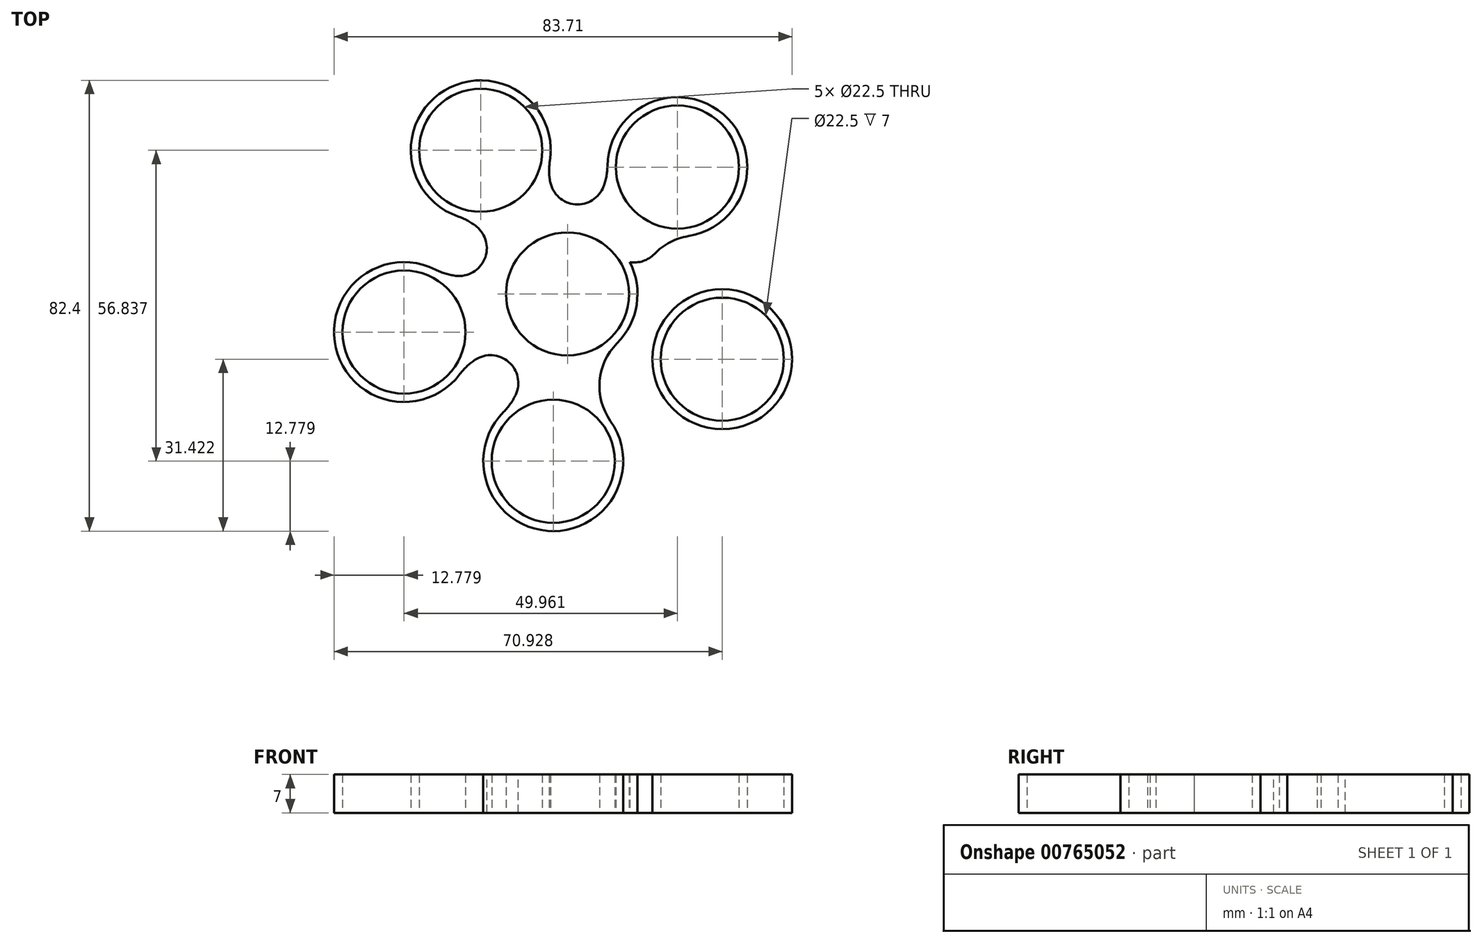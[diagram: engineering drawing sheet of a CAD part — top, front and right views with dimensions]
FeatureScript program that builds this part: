
annotation { "Feature Type Name" : "Feature", "Feature Type Description" : "" }
export const myFeature = defineFeature(function(context is Context, id is Id, definition is map)
    precondition{}
    {
        {
            var Q0;
            Q0=qCreatedBy(makeId("Top.planeOp"),FACE);
            var sketch = newSketch(context, id + "F0", { "sketchPlane" : qUnion([Q0])});
            skCircle(sketch, "E0", {"center": v(0, 0) * mm, "radius": 12.78 * mm});
            skCircle(sketch, "E1", {"center": v(20.08, 23.2) * mm, "radius": 12.78 * mm});
            skArc(sketch, "E2", {"start": v(22.1, 10.58) * mm, "mid": v(15.48, 6.89) * mm, "end": v(12.78, -0.2) * mm});
            skArc(sketch, "E3.MirrorCS", {"start": v(7.3, 23.4) * mm, "mid": v(4.6, 16.31) * mm, "end": v(-2.03, 12.62) * mm});
            skCircle(sketch, "E4", {"center": v(0, 0) * mm, "radius": 11.25 * mm});
            skCircle(sketch, "E5", {"center": v(20.08, 23.2) * mm, "radius": 11.25 * mm});
            skCircle(sketch, "E6.1.0", {"center": v(-15.86, 26.27) * mm, "radius": 11.25 * mm});
            skCircle(sketch, "E6.1.1", {"center": v(-15.86, 26.27) * mm, "radius": 12.78 * mm});
            skArc(sketch, "E6.1.2", {"start": v(-3.23, 24.3) * mm, "mid": v(-1.76, 16.85) * mm, "end": v(4.14, 12.1) * mm});
            skArc(sketch, "E6.1.3", {"start": v(-20, 14.17) * mm, "mid": v(-14.1, 9.41) * mm, "end": v(-12.63, 1.97) * mm});
            skCircle(sketch, "E6.2.0", {"center": v(-29.88, -6.97) * mm, "radius": 11.25 * mm});
            skCircle(sketch, "E6.2.1", {"center": v(-29.88, -6.97) * mm, "radius": 12.78 * mm});
            skArc(sketch, "E6.2.2", {"start": v(-24.1, 4.44) * mm, "mid": v(-16.58, 3.53) * mm, "end": v(-10.23, 7.67) * mm});
            skArc(sketch, "E6.2.3", {"start": v(-19.65, -14.64) * mm, "mid": v(-13.3, -10.5) * mm, "end": v(-5.78, -11.4) * mm});
            skCircle(sketch, "E6.3.0", {"center": v(-2.6, -30.57) * mm, "radius": 11.25 * mm});
            skCircle(sketch, "E6.3.1", {"center": v(-2.6, -30.57) * mm, "radius": 12.78 * mm});
            skArc(sketch, "E6.3.2", {"start": v(-11.67, -21.55) * mm, "mid": v(-8.48, -14.67) * mm, "end": v(-10.46, -7.35) * mm});
            skArc(sketch, "E6.3.3", {"start": v(7.85, -23.22) * mm, "mid": v(5.87, -15.9) * mm, "end": v(9.06, -9.02) * mm});
            skCircle(sketch, "E6.4.0", {"center": v(28.27, -11.93) * mm, "radius": 11.25 * mm});
            skCircle(sketch, "E6.4.1", {"center": v(28.27, -11.93) * mm, "radius": 12.78 * mm});
            skArc(sketch, "E6.4.2", {"start": v(16.89, -17.76) * mm, "mid": v(11.33, -12.6) * mm, "end": v(3.76, -12.22) * mm});
            skArc(sketch, "E6.4.3", {"start": v(24.5, 0.29) * mm, "mid": v(16.93, 0.67) * mm, "end": v(11.38, 5.83) * mm});
            skSolve(sketch);
        }
        {
            var Q0;
            {var subQ3=sQuery(id+"F0.wireOp",EDGE,"E3.MirrorCS");var subQ7=sQuery(id+"F0.wireOp",EDGE,"E0");var subQ8=makeQuery(id+"F0.imprint","INTERSECT",VERTEX,{"derivedFrom":[subQ7,subQ3]});Q0=makeQuery(id+"F0.imprint","IMPRINT",FACE,{"disambiguationData":[TD([[makeQuery(id+"F0.imprint","IMPRINT",EDGE,{"disambiguationData":[TD([[subQ8,-1.0]])],"derivedFrom":subQ7}),-1.0]])]});}
            var Q1;
            {var subQ1=sQuery(id+"F0.wireOp",EDGE,"E0");var subQ13=makeQuery(id+"F0.imprint","INTERSECT",VERTEX,{"derivedFrom":[subQ1,sQuery(id+"F0.wireOp",EDGE,"E6.1.2")]});Q1=makeQuery(id+"F0.imprint","IMPRINT",FACE,{"disambiguationData":[TD([[makeQuery(id+"F0.imprint","IMPRINT",EDGE,{"disambiguationData":[TD([[subQ13,1.0]])],"derivedFrom":subQ1}),1.0]])]});}
            var Q2;
            {var subQ0=sQuery(id+"F0.wireOp",EDGE,"E3.MirrorCS");var subQ1=sQuery(id+"F0.wireOp",EDGE,"E0");var subQ2=makeQuery(id+"F0.imprint","INTERSECT",VERTEX,{"derivedFrom":[subQ1,subQ0]});Q2=makeQuery(id+"F0.imprint","IMPRINT",FACE,{"disambiguationData":[TD([[makeQuery(id+"F0.imprint","IMPRINT",EDGE,{"disambiguationData":[TD([[subQ2,1.0]])],"derivedFrom":subQ1}),-1.0]])]});}
            var Q3;
            {var subQ1=sQuery(id+"F0.wireOp",EDGE,"E0");var subQ3=sQuery(id+"F0.wireOp",EDGE,"E6.4.3");var subQ4=makeQuery(id+"F0.imprint","INTERSECT",VERTEX,{"derivedFrom":[subQ1,subQ3]});Q3=makeQuery(id+"F0.imprint","IMPRINT",FACE,{"disambiguationData":[TD([[makeQuery(id+"F0.imprint","IMPRINT",EDGE,{"disambiguationData":[TD([[subQ4,1.0]])],"derivedFrom":subQ3}),1.0]])]});}
            var Q4;
            {var subQ1=sQuery(id+"F0.wireOp",EDGE,"E0");var subQ8=makeQuery(id+"F0.imprint","INTERSECT",VERTEX,{"derivedFrom":[subQ1,sQuery(id+"F0.wireOp",EDGE,"E6.4.3")]});Q4=makeQuery(id+"F0.imprint","IMPRINT",FACE,{"disambiguationData":[TD([[makeQuery(id+"F0.imprint","IMPRINT",EDGE,{"disambiguationData":[TD([[subQ8,-1.0]])],"derivedFrom":subQ1}),1.0]])]});}
            var Q5;
            {var subQ0=sQuery(id+"F0.wireOp",EDGE,"E6.1.3");var subQ1=sQuery(id+"F0.wireOp",EDGE,"E0");var subQ2=makeQuery(id+"F0.imprint","INTERSECT",VERTEX,{"derivedFrom":[subQ1,subQ0]});Q5=makeQuery(id+"F0.imprint","IMPRINT",FACE,{"disambiguationData":[TD([[makeQuery(id+"F0.imprint","IMPRINT",EDGE,{"disambiguationData":[TD([[subQ2,1.0]])],"derivedFrom":subQ1}),-1.0]])]});}
            var Q6;
            {var subQ3=sQuery(id+"F0.wireOp",EDGE,"E6.1.3");var subQ7=sQuery(id+"F0.wireOp",EDGE,"E0");var subQ8=makeQuery(id+"F0.imprint","INTERSECT",VERTEX,{"derivedFrom":[subQ7,subQ3]});Q6=makeQuery(id+"F0.imprint","IMPRINT",FACE,{"disambiguationData":[TD([[makeQuery(id+"F0.imprint","IMPRINT",EDGE,{"disambiguationData":[TD([[subQ8,-1.0]])],"derivedFrom":subQ7}),-1.0]])]});}
            var Q7;
            {var subQ5=sQuery(id+"F0.wireOp",EDGE,"E6.4.3");var subQ7=sQuery(id+"F0.wireOp",EDGE,"E0");var subQ9=makeQuery(id+"F0.imprint","INTERSECT",VERTEX,{"derivedFrom":[subQ7,subQ5]});Q7=makeQuery(id+"F0.imprint","IMPRINT",FACE,{"disambiguationData":[TD([[makeQuery(id+"F0.imprint","IMPRINT",EDGE,{"disambiguationData":[TD([[subQ9,-1.0]])],"derivedFrom":subQ7}),-1.0]])]});}
            var Q8;
            {var subQ6=sQuery(id+"F0.wireOp",EDGE,"E0");var subQ9=sQuery(id+"F0.wireOp",EDGE,"E6.3.3");var subQ10=makeQuery(id+"F0.imprint","INTERSECT",VERTEX,{"derivedFrom":[subQ6,subQ9]});Q8=makeQuery(id+"F0.imprint","IMPRINT",FACE,{"disambiguationData":[TD([[makeQuery(id+"F0.imprint","IMPRINT",EDGE,{"disambiguationData":[TD([[subQ10,1.0]])],"derivedFrom":subQ9}),-1.0]])]});}
            var Q9;
            {var subQ3=sQuery(id+"F0.wireOp",EDGE,"E6.1.2");var subQ5=sQuery(id+"F0.wireOp",EDGE,"E0");var subQ6=makeQuery(id+"F0.imprint","INTERSECT",VERTEX,{"derivedFrom":[subQ5,subQ3]});Q9=makeQuery(id+"F0.imprint","IMPRINT",FACE,{"disambiguationData":[TD([[makeQuery(id+"F0.imprint","IMPRINT",EDGE,{"disambiguationData":[TD([[subQ6,1.0]])],"derivedFrom":subQ5}),-1.0]])]});}
            var Q10;
            {var subQ0=sQuery(id+"F0.wireOp",EDGE,"E6.3.3");var subQ1=sQuery(id+"F0.wireOp",EDGE,"E0");var subQ2=makeQuery(id+"F0.imprint","INTERSECT",VERTEX,{"derivedFrom":[subQ1,subQ0]});Q10=makeQuery(id+"F0.imprint","IMPRINT",FACE,{"disambiguationData":[TD([[makeQuery(id+"F0.imprint","IMPRINT",EDGE,{"disambiguationData":[TD([[subQ2,1.0]])],"derivedFrom":subQ1}),-1.0]])]});}
            var Q11;
            {var subQ0=sQuery(id+"F0.wireOp",EDGE,"E6.2.3");var subQ1=sQuery(id+"F0.wireOp",EDGE,"E0");var subQ2=makeQuery(id+"F0.imprint","INTERSECT",VERTEX,{"derivedFrom":[subQ1,subQ0]});Q11=makeQuery(id+"F0.imprint","IMPRINT",FACE,{"disambiguationData":[TD([[makeQuery(id+"F0.imprint","IMPRINT",EDGE,{"disambiguationData":[TD([[subQ2,1.0]])],"derivedFrom":subQ1}),-1.0]])]});}
            var Q12;
            {var subQ3=sQuery(id+"F0.wireOp",EDGE,"E6.2.3");var subQ5=sQuery(id+"F0.wireOp",EDGE,"E0");var subQ6=makeQuery(id+"F0.imprint","INTERSECT",VERTEX,{"derivedFrom":[subQ5,subQ3]});Q12=makeQuery(id+"F0.imprint","IMPRINT",FACE,{"disambiguationData":[TD([[makeQuery(id+"F0.imprint","IMPRINT",EDGE,{"disambiguationData":[TD([[subQ6,-1.0]])],"derivedFrom":subQ5}),-1.0]])]});}
            var Q13;
            Q13=makeQuery(id+"F0.imprint","IMPRINT",FACE,{"disambiguationData":[TD([[makeQuery(id+"F0.imprint","IMPRINT",EDGE,{"derivedFrom":sQuery(id+"F0.wireOp",EDGE,"E6.4.0")}),-1.0]])]});
            var Q14;
            Q14=makeQuery(id+"F0.imprint","IMPRINT",FACE,{"disambiguationData":[TD([[makeQuery(id+"F0.imprint","IMPRINT",EDGE,{"derivedFrom":sQuery(id+"F0.wireOp",EDGE,"E6.3.0")}),-1.0]])]});
            var Q15;
            Q15=makeQuery(id+"F0.imprint","IMPRINT",FACE,{"disambiguationData":[TD([[makeQuery(id+"F0.imprint","IMPRINT",EDGE,{"derivedFrom":sQuery(id+"F0.wireOp",EDGE,"E6.2.0")}),-1.0]])]});
            var Q16;
            Q16=makeQuery(id+"F0.imprint","IMPRINT",FACE,{"disambiguationData":[TD([[makeQuery(id+"F0.imprint","IMPRINT",EDGE,{"derivedFrom":sQuery(id+"F0.wireOp",EDGE,"E6.1.0")}),-1.0]])]});
            var Q17;
            {var subQ0=sQuery(id+"F0.wireOp",EDGE,"xdie79fZ-8WdW-vPre-LFcJ-lH0hnhuQZrEy");var subQ5=sQuery(id+"F0.wireOp",EDGE,"E5");var subQ6=makeQuery(id+"F0.imprint","INTERSECT",VERTEX,{"derivedFrom":[subQ0,subQ5]});Q17=makeQuery(id+"F0.imprint","IMPRINT",FACE,{"disambiguationData":[TD([[makeQuery(id+"F0.imprint","IMPRINT",EDGE,{"disambiguationData":[TD([[subQ6,1.0]])],"derivedFrom":subQ5}),-1.0]])]});}
            var Q18;
            {var subQ1=sQuery(id+"F0.wireOp",EDGE,"E1");var subQ3=sQuery(id+"F0.wireOp",EDGE,"9D55kv2u-RZAq-n16d-mXt5-XkmHfy5zVu7U");var subQ4=makeQuery(id+"F0.imprint","INTERSECT",VERTEX,{"derivedFrom":[subQ1,subQ3]});Q18=makeQuery(id+"F0.imprint","IMPRINT",FACE,{"disambiguationData":[TD([[makeQuery(id+"F0.imprint","IMPRINT",EDGE,{"disambiguationData":[TD([[subQ4,-1.0]])],"derivedFrom":subQ3}),1.0]])]});}
            var Q19;
            {var subQ1=sQuery(id+"F0.wireOp",EDGE,"E1");var subQ3=sQuery(id+"F0.wireOp",EDGE,"9D55kv2u-RZAq-n16d-mXt5-XkmHfy5zVu7U");var subQ4=makeQuery(id+"F0.imprint","INTERSECT",VERTEX,{"derivedFrom":[subQ1,subQ3]});Q19=makeQuery(id+"F0.imprint","IMPRINT",FACE,{"disambiguationData":[TD([[makeQuery(id+"F0.imprint","IMPRINT",EDGE,{"disambiguationData":[TD([[subQ4,-1.0]])],"derivedFrom":subQ3}),-1.0]])]});}
            var Q20;
            Q20=makeQuery(id+"F0.imprint","IMPRINT",FACE,{"disambiguationData":[TD([[makeQuery(id+"F0.imprint","IMPRINT",EDGE,{"derivedFrom":sQuery(id+"F0.wireOp",EDGE,"E5")}),-1.0]])]});
            extrude(context, id + "F1", {"entities" : qUnion([Q0, Q1, Q2, Q3, Q4, Q5, Q6, Q7, Q8, Q9, Q10, Q11, Q12, Q13, Q14, Q15, Q16, Q17, Q18, Q19, Q20]), "depth" : 7 * mm, "offsetDistance" : 25.4 * mm});
        }
        {
            var Q0;
            Q0=makeQuery(id+"F1.opExtrude","SWEPT_EDGE",EDGE,{"disambiguationData":[OSD([sQuery(id+"F0.wireOp",EDGE,"E6.3.3"),sQuery(id+"F0.wireOp",EDGE,"E6.4.2")])]});
            var Q1;
            Q1=makeQuery(id+"F1.opExtrude","SWEPT_EDGE",EDGE,{"disambiguationData":[OSD([sQuery(id+"F0.wireOp",EDGE,"E6.2.3"),sQuery(id+"F0.wireOp",EDGE,"E6.3.2")])]});
            var Q2;
            Q2=makeQuery(id+"F1.opExtrude","SWEPT_EDGE",EDGE,{"disambiguationData":[OSD([sQuery(id+"F0.wireOp",EDGE,"E6.1.3"),sQuery(id+"F0.wireOp",EDGE,"E6.2.2")])]});
            var Q3;
            Q3=makeQuery(id+"F1.opExtrude","SWEPT_EDGE",EDGE,{"disambiguationData":[OSD([sQuery(id+"F0.wireOp",EDGE,"E3.MirrorCS"),sQuery(id+"F0.wireOp",EDGE,"E6.1.2")])]});
            var Q4;
            Q4=makeQuery(id+"F1.opExtrude","SWEPT_EDGE",EDGE,{"disambiguationData":[OSD([sQuery(id+"F0.wireOp",EDGE,"E2"),sQuery(id+"F0.wireOp",EDGE,"E6.4.3")])]});
            fillet(context, id + "F2", {"entities" : qUnion([Q0, Q1, Q2, Q3, Q4]), "radius" : 5.08 * mm, "tangentPropagation" : true, "allowEdgeOverflow" : false});
        }
    });
